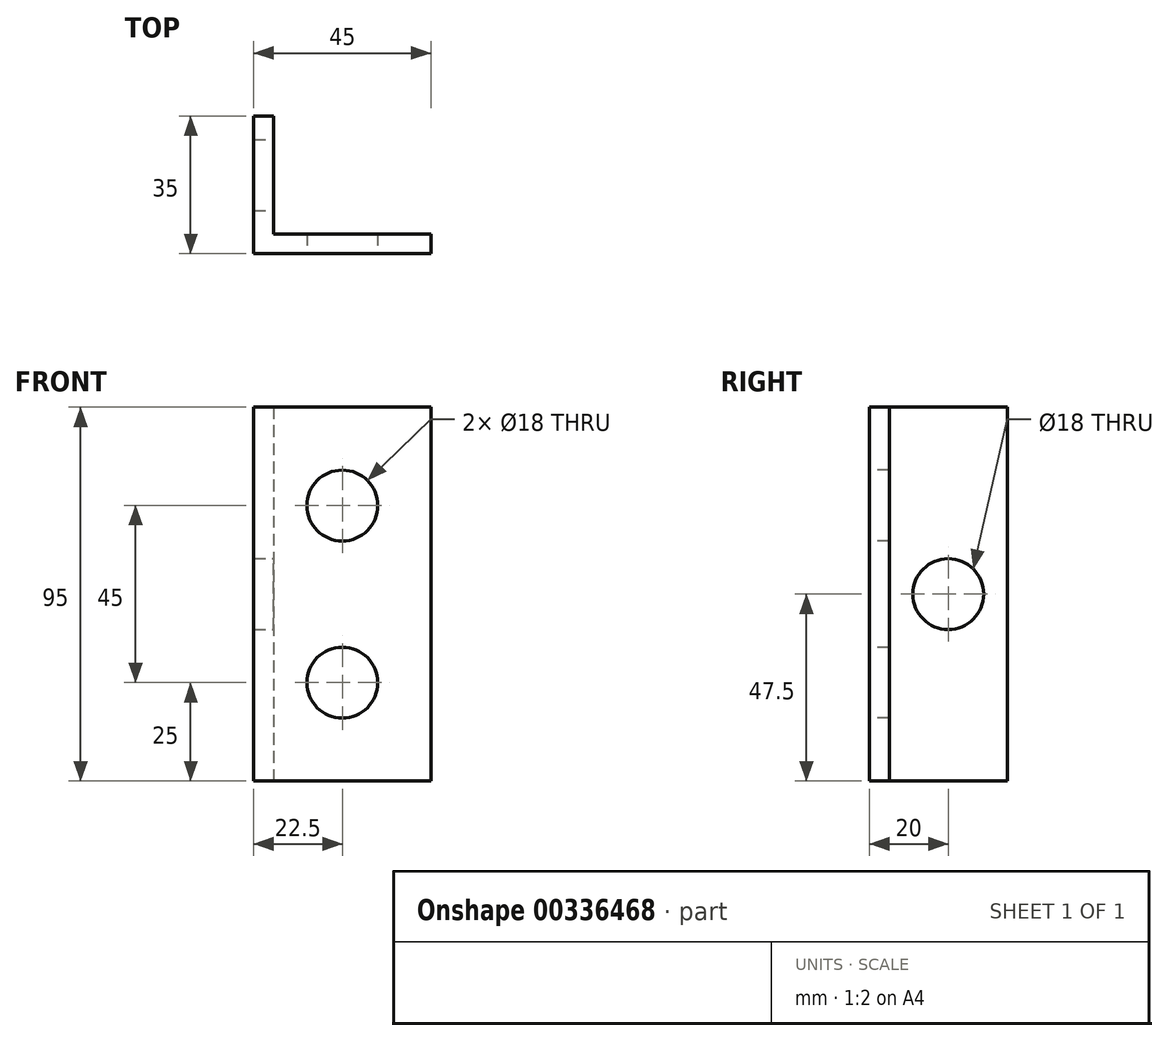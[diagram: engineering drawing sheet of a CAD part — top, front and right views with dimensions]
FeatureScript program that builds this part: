
annotation { "Feature Type Name" : "Feature", "Feature Type Description" : "" }
export const myFeature = defineFeature(function(context is Context, id is Id, definition is map)
    precondition{}
    {
        {
            var Q0;
            Q0=qCreatedBy(makeId("Top.planeOp"),FACE);
            var sketch = newSketch(context, id + "F0", { "sketchPlane" : qUnion([Q0])});
            skLineSegment(sketch, "E0", {"start": v(0, 30) * mm, "end": v(0, 0) * mm});
            skLineSegment(sketch, "E1", {"start": v(0, 0) * mm, "end": v(40, 0) * mm});
            skLineSegment(sketch, "E2", {"start": v(0, 30) * mm, "end": v(-5, 30) * mm});
            skLineSegment(sketch, "E3", {"start": v(-5, 30) * mm, "end": v(-5, -5) * mm});
            skLineSegment(sketch, "E4", {"start": v(-5, -5) * mm, "end": v(40, -5) * mm});
            skLineSegment(sketch, "E5", {"start": v(40, 0) * mm, "end": v(40, -5) * mm});
            skSolve(sketch);
        }
        {
            var Q0;
            Q0=makeQuery(id+"F0.imprint","IMPRINT",FACE,{"disambiguationData":[TD([[makeQuery(id+"F0.imprint","IMPRINT",EDGE,{"derivedFrom":sQuery(id+"F0.wireOp",EDGE,"E0")}),-1.0]])]});
            extrude(context, id + "F1", {"entities" : qUnion([Q0]), "depth" : 95 * mm});
        }
        {
            var Q0;
            Q0=makeQuery(id+"F1.opExtrude","SWEPT_FACE",FACE,{"disambiguationData":[OSD([sQuery(id+"F0.wireOp",EDGE,"E4")])]});
            var sketch = newSketch(context, id + "F2", { "sketchPlane" : qUnion([Q0])});
            skCircle(sketch, "E6", {"center": v(17.5, 70) * mm, "radius": 9 * mm});
            skCircle(sketch, "E7", {"center": v(17.5, 25) * mm, "radius": 9 * mm});
            skSolve(sketch);
        }
        {
            var Q0;
            Q0 = qSketchRegion(id + "F2", true);
            extrude(context, id + "F3", {"entities" : qUnion([Q0]), "operationType" : NewBodyOperationType.REMOVE, "oppositeDirection" : true, "depth" : 25 * mm});
        }
        {
            var Q0;
            Q0=makeQuery(id+"F1.opExtrude","SWEPT_FACE",FACE,{"disambiguationData":[OSD([sQuery(id+"F0.wireOp",EDGE,"E0")])]});
            var sketch = newSketch(context, id + "F4", { "sketchPlane" : qUnion([Q0])});
            skCircle(sketch, "E8", {"center": v(15, 47.5) * mm, "radius": 9 * mm});
            skSolve(sketch);
        }
        {
            var Q0;
            Q0 = qSketchRegion(id + "F4", true);
            extrude(context, id + "F5", {"entities" : qUnion([Q0]), "operationType" : NewBodyOperationType.REMOVE, "oppositeDirection" : true, "depth" : 25 * mm});
        }
    });
